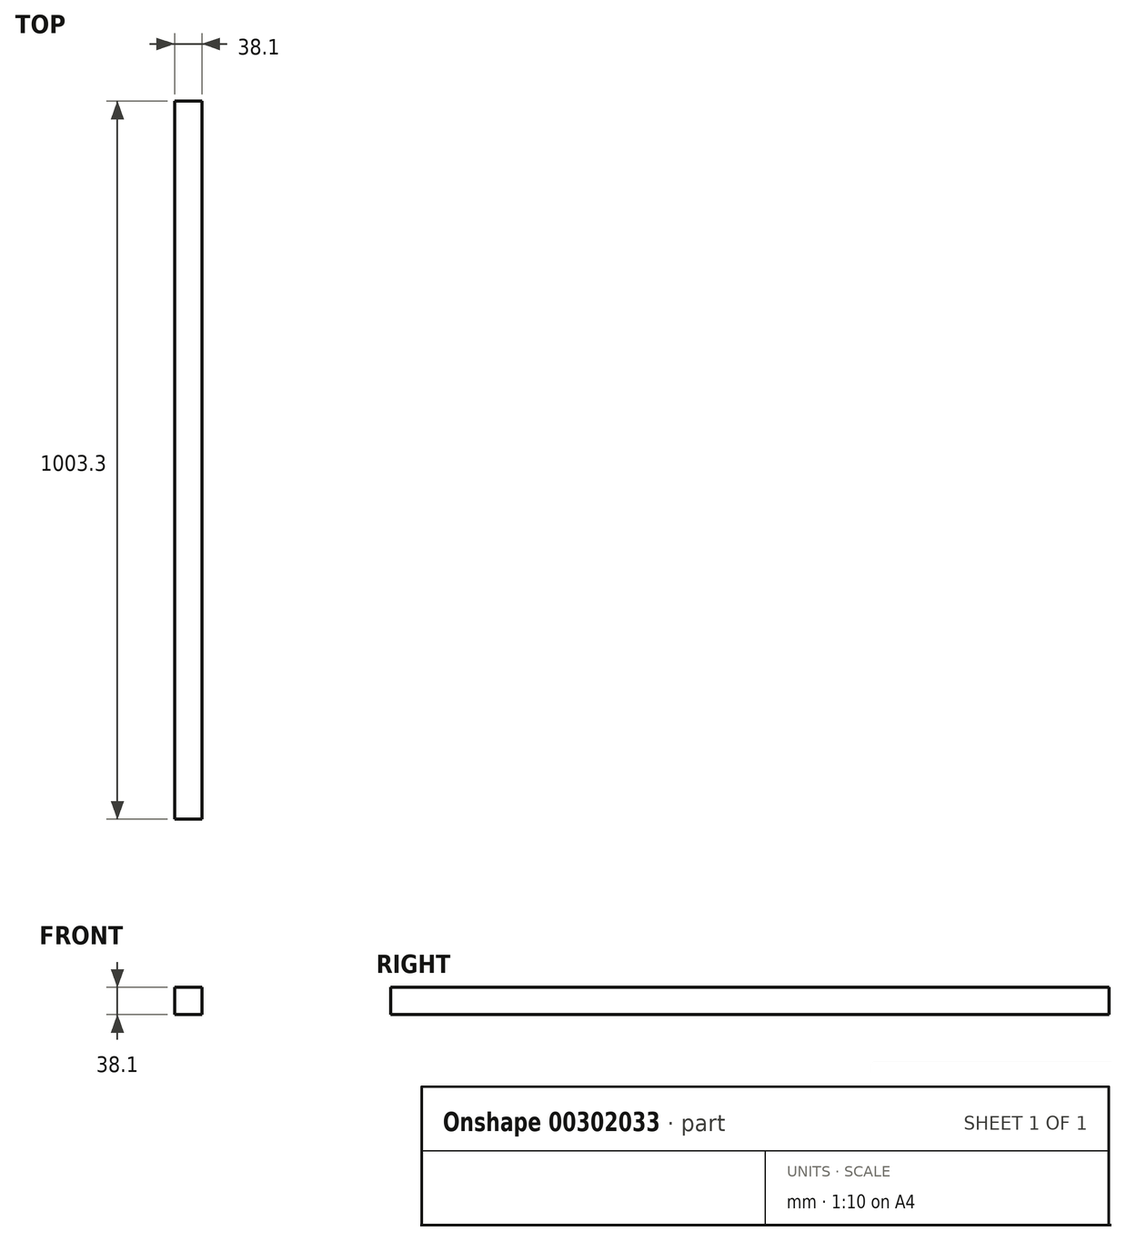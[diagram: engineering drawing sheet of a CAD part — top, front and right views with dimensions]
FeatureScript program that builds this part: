
annotation { "Feature Type Name" : "Feature", "Feature Type Description" : "" }
export const myFeature = defineFeature(function(context is Context, id is Id, definition is map)
    precondition{}
    {
        {
            var Q0;
            Q0=qCreatedBy(makeId("Front.planeOp"),FACE);
            var sketch = newSketch(context, id + "F0", { "sketchPlane" : qUnion([Q0])});
            skLineSegment(sketch, "E0.bottom", {"start": v(0, 0) * mm, "end": v(38.1, 0) * mm});
            skLineSegment(sketch, "E0.top", {"start": v(0, 38.1) * mm, "end": v(38.1, 38.1) * mm});
            skLineSegment(sketch, "E0.left", {"start": v(0, 0) * mm, "end": v(0, 38.1) * mm});
            skLineSegment(sketch, "E0.right", {"start": v(38.1, 0) * mm, "end": v(38.1, 38.1) * mm});
            skSolve(sketch);
        }
        {
            var Q0;
            Q0 = qSketchRegion(id + "F0", true);
            extrude(context, id + "F1", {"entities" : qUnion([Q0]), "depth" : 1003.3 * mm});
        }
    });
